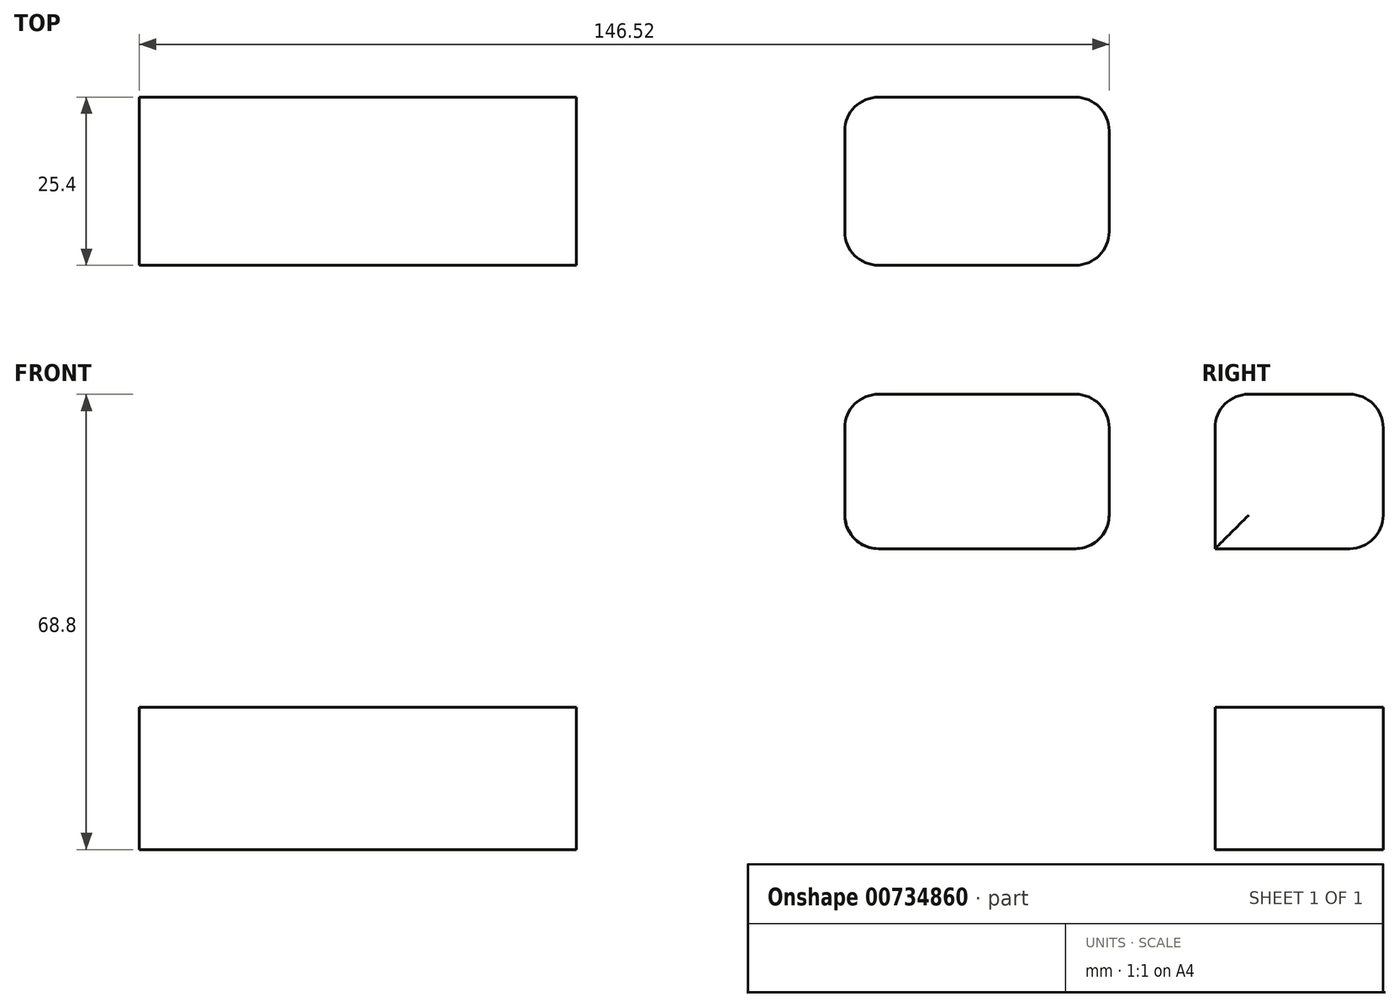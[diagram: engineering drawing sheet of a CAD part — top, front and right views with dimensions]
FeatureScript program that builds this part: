
annotation { "Feature Type Name" : "Feature", "Feature Type Description" : "" }
export const myFeature = defineFeature(function(context is Context, id is Id, definition is map)
    precondition{}
    {
        {
            var Q0;
            Q0=qCreatedBy(makeId("Front.planeOp"),FACE);
            var sketch = newSketch(context, id + "F0", { "sketchPlane" : qUnion([Q0])});
            skLineSegment(sketch, "E0.bottom", {"start": v(33.02, 10.75) * mm, "end": v(-33.02, 10.75) * mm});
            skLineSegment(sketch, "E0.top", {"start": v(33.02, -10.75) * mm, "end": v(-33.02, -10.75) * mm});
            skLineSegment(sketch, "E0.left", {"start": v(33.02, 10.75) * mm, "end": v(33.02, -10.75) * mm});
            skLineSegment(sketch, "E0.right", {"start": v(-33.02, 10.75) * mm, "end": v(-33.02, -10.75) * mm});
            skPoint(sketch, "E0.middle", {"position": v(0, 0) * mm});
            skLineSegment(sketch, "E1.bottom", {"start": v(113.5, 58.05) * mm, "end": v(73.56, 58.05) * mm});
            skLineSegment(sketch, "E1.top", {"start": v(113.5, 34.7) * mm, "end": v(73.56, 34.7) * mm});
            skLineSegment(sketch, "E1.left", {"start": v(113.5, 58.05) * mm, "end": v(113.5, 34.7) * mm});
            skLineSegment(sketch, "E1.right", {"start": v(73.56, 58.05) * mm, "end": v(73.56, 34.7) * mm});
            skPoint(sketch, "E1.middle", {"position": v(93.53, 46.38) * mm});
            skLineSegment(sketch, "E2", {"start": v(33.02, 10.75) * mm, "end": v(33.02, 27.95) * mm});
            skArc(sketch, "E3", {"start": v(33.02, 27.95) * mm, "mid": v(44.03, 46.16) * mm, "end": v(65.27, 44.85) * mm});
            skLineSegment(sketch, "E4", {"start": v(65.27, 44.85) * mm, "end": v(76.82, 36.85) * mm});
            skSolve(sketch);
        }
        {
            var Q0;
            Q0=makeQuery(id+"F0.imprint","IMPRINT",FACE,{"disambiguationData":[TD([[makeQuery(id+"F0.imprint","IMPRINT",EDGE,{"derivedFrom":sQuery(id+"F0.wireOp",EDGE,"E0.bottom")}),1.0]])]});
            var Q1;
            {var subQ0=sQuery(id+"F0.wireOp",EDGE,"E1.bottom");Q1=makeQuery(id+"F0.imprint","IMPRINT",FACE,{"disambiguationData":[TD([[makeQuery(id+"F0.imprint","IMPRINT",EDGE,{"derivedFrom":subQ0}),1.0]])]});}
            extrude(context, id + "F1", {"entities" : qUnion([Q0, Q1]), "depth" : 25.4 * mm, "offsetDistance" : 25.4 * mm});
        }
        {
            var Q0;
            Q0=makeQuery(id+"F1.opExtrude","CAP_EDGE",EDGE,{"disambiguationData":[OSD([sQuery(id+"F0.wireOp",EDGE,"E1.left")])],"isStart":true});
            var Q1;
            Q1=makeQuery(id+"F1.opExtrude","CAP_EDGE",EDGE,{"disambiguationData":[OSD([sQuery(id+"F0.wireOp",EDGE,"E1.left")])],"isStart":false});
            var Q2;
            Q2=makeQuery(id+"F1.opExtrude","SWEPT_EDGE",EDGE,{"disambiguationData":[OSD([sQuery(id+"F0.wireOp",EDGE,"E1.top"),sQuery(id+"F0.wireOp",EDGE,"E1.left")])]});
            var Q3;
            Q3=makeQuery(id+"F1.opExtrude","SWEPT_EDGE",EDGE,{"disambiguationData":[OSD([sQuery(id+"F0.wireOp",EDGE,"E1.bottom"),sQuery(id+"F0.wireOp",EDGE,"E1.left")])]});
            var Q4;
            Q4=makeQuery(id+"F1.opExtrude","CAP_EDGE",EDGE,{"disambiguationData":[OSD([sQuery(id+"F0.wireOp",EDGE,"E1.bottom")])],"isStart":true});
            var Q5;
            Q5=makeQuery(id+"F1.opExtrude","CAP_EDGE",EDGE,{"disambiguationData":[OSD([sQuery(id+"F0.wireOp",EDGE,"E1.top")])],"isStart":true});
            var Q6;
            Q6=makeQuery(id+"F1.opExtrude","CAP_EDGE",EDGE,{"disambiguationData":[OSD([sQuery(id+"F0.wireOp",EDGE,"E1.right")])],"isStart":true});
            var Q7;
            Q7=makeQuery(id+"F1.opExtrude","SWEPT_EDGE",EDGE,{"disambiguationData":[OSD([sQuery(id+"F0.wireOp",EDGE,"E1.bottom"),sQuery(id+"F0.wireOp",EDGE,"E1.right")])]});
            var Q8;
            Q8=makeQuery(id+"F1.opExtrude","CAP_EDGE",EDGE,{"disambiguationData":[OSD([sQuery(id+"F0.wireOp",EDGE,"E1.right")])],"isStart":false});
            var Q9;
            Q9=makeQuery(id+"F1.opExtrude","SWEPT_EDGE",EDGE,{"disambiguationData":[OSD([sQuery(id+"F0.wireOp",EDGE,"E1.top"),sQuery(id+"F0.wireOp",EDGE,"E1.right")])]});
            var Q10;
            Q10=makeQuery(id+"F1.opExtrude","CAP_EDGE",EDGE,{"disambiguationData":[OSD([sQuery(id+"F0.wireOp",EDGE,"E1.bottom")])],"isStart":false});
            fillet(context, id + "F2", {"entities" : qUnion([Q0, Q1, Q2, Q3, Q4, Q5, Q6, Q7, Q8, Q9, Q10]), "radius" : 5.08 * mm, "tangentPropagation" : true, "allowEdgeOverflow" : false});
        }
    });
